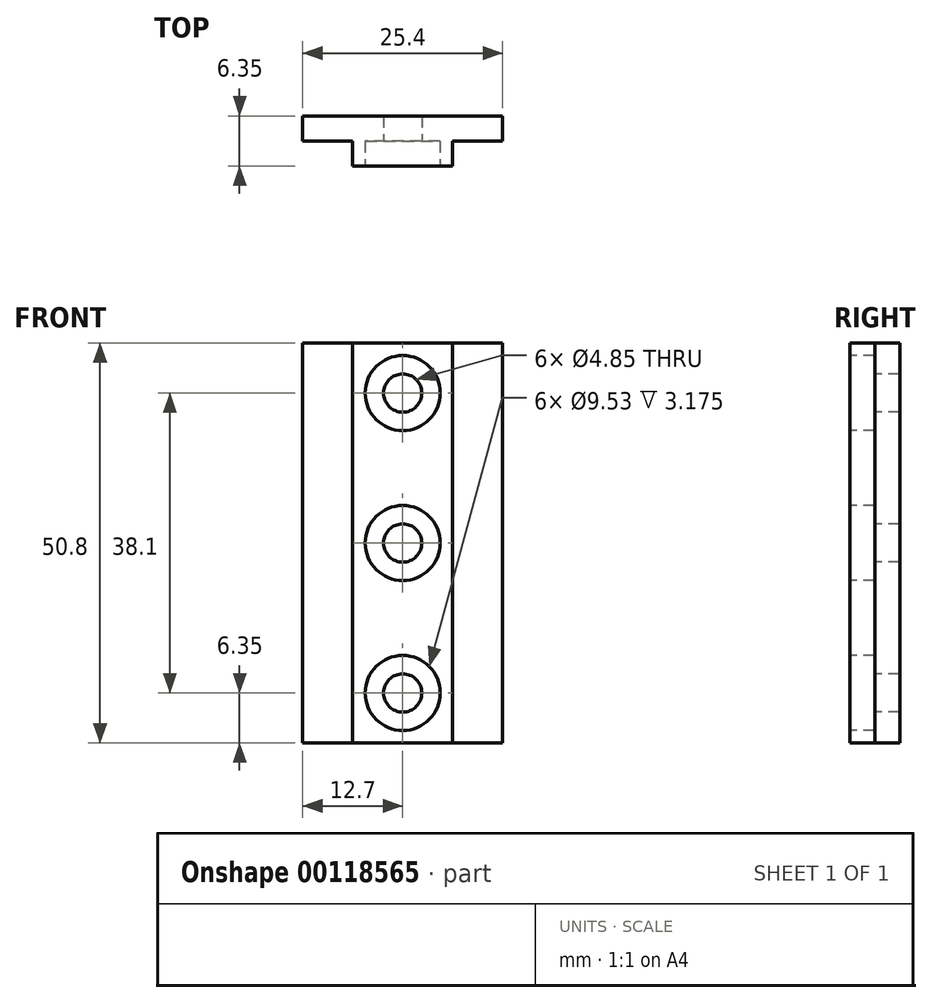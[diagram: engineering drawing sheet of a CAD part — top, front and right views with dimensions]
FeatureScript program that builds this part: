
annotation { "Feature Type Name" : "Feature", "Feature Type Description" : "" }
export const myFeature = defineFeature(function(context is Context, id is Id, definition is map)
    precondition{}
    {
        {
            var Q0;
            Q0=qCreatedBy(makeId("Front.planeOp"),FACE);
            var sketch = newSketch(context, id + "F0", { "sketchPlane" : qUnion([Q0])});
            skLineSegment(sketch, "E0.bottom", {"start": v(12.7, 25.4) * mm, "end": v(-12.7, 25.4) * mm});
            skLineSegment(sketch, "E0.top", {"start": v(12.7, -25.4) * mm, "end": v(-12.7, -25.4) * mm});
            skLineSegment(sketch, "E0.left", {"start": v(12.7, 25.4) * mm, "end": v(12.7, -25.4) * mm});
            skLineSegment(sketch, "E0.right", {"start": v(-12.7, 25.4) * mm, "end": v(-12.7, -25.4) * mm});
            skPoint(sketch, "E0.middle", {"position": v(0, 0) * mm});
            skSolve(sketch);
        }
        {
            var Q0;
            Q0 = qSketchRegion(id + "F0", true);
            extrude(context, id + "F1", {"entities" : qUnion([Q0]), "depth" : 6.35 * mm});
        }
        {
            var Q0;
            Q0=makeQuery(id+"F1.opExtrude","CAP_FACE",FACE,{"disambiguationData":[OSD([sQuery(id+"F0.wireOp",EDGE,"E0.bottom"),sQuery(id+"F0.wireOp",EDGE,"E0.top"),sQuery(id+"F0.wireOp",EDGE,"E0.left"),sQuery(id+"F0.wireOp",EDGE,"E0.right")])],"isStart":false});
            var sketch = newSketch(context, id + "F2", { "sketchPlane" : qUnion([Q0])});
            skLineSegment(sketch, "E1.bottom", {"start": v(6.35, 25.4) * mm, "end": v(-6.35, 25.4) * mm});
            skLineSegment(sketch, "E1.top", {"start": v(6.35, -25.4) * mm, "end": v(-6.35, -25.4) * mm});
            skLineSegment(sketch, "E1.left", {"start": v(6.35, 25.4) * mm, "end": v(6.35, -25.4) * mm});
            skLineSegment(sketch, "E1.right", {"start": v(-6.35, 25.4) * mm, "end": v(-6.35, -25.4) * mm});
            skPoint(sketch, "E1.middle", {"position": v(0, 0) * mm});
            skSolve(sketch);
        }
        {
            var Q0;
            {var subQ0=sQuery(id+"F2.wireOp",EDGE,"E1.right");Q0=makeQuery(id+"F2.imprint","IMPRINT",FACE,{"disambiguationData":[TD([[makeQuery(id+"F2.imprint","IMPRINT",EDGE,{"derivedFrom":subQ0}),-1.0]])]});}
            var Q1;
            {var subQ0=sQuery(id+"F2.wireOp",EDGE,"E1.left");Q1=makeQuery(id+"F2.imprint","IMPRINT",FACE,{"disambiguationData":[TD([[makeQuery(id+"F2.imprint","IMPRINT",EDGE,{"derivedFrom":subQ0}),1.0]])]});}
            extrude(context, id + "F3", {"entities" : qUnion([Q0, Q1]), "operationType" : NewBodyOperationType.REMOVE, "oppositeDirection" : true, "depth" : 3.17 * mm});
        }
        {
            var Q0;
            Q0=makeQuery(id+"F1.opExtrude","CAP_FACE",FACE,{"disambiguationData":[OSD([sQuery(id+"F0.wireOp",EDGE,"E0.bottom"),sQuery(id+"F0.wireOp",EDGE,"E0.top"),sQuery(id+"F0.wireOp",EDGE,"E0.left"),sQuery(id+"F0.wireOp",EDGE,"E0.right")])],"isStart":false});
            var sketch = newSketch(context, id + "F4", { "sketchPlane" : qUnion([Q0])});
            skCircle(sketch, "E2", {"center": v(0, 0) * mm, "radius": 2.43 * mm});
            skCircle(sketch, "E3", {"center": v(0, 19.05) * mm, "radius": 2.43 * mm});
            skCircle(sketch, "E4.MirrorC", {"center": v(0, -19.05) * mm, "radius": 2.43 * mm});
            skSolve(sketch);
        }
        {
            var Q0;
            Q0 = qSketchRegion(id + "F4", true);
            extrude(context, id + "F5", {"entities" : qUnion([Q0]), "operationType" : NewBodyOperationType.REMOVE, "endBound" : BoundingType.THROUGH_ALL, "oppositeDirection" : true, "depth" : 3.17 * mm});
        }
        {
            var Q0;
            Q0=makeQuery(id+"F1.opExtrude","CAP_FACE",FACE,{"disambiguationData":[OSD([sQuery(id+"F0.wireOp",EDGE,"E0.bottom"),sQuery(id+"F0.wireOp",EDGE,"E0.top"),sQuery(id+"F0.wireOp",EDGE,"E0.left"),sQuery(id+"F0.wireOp",EDGE,"E0.right")])],"isStart":false});
            var sketch = newSketch(context, id + "F6", { "sketchPlane" : qUnion([Q0])});
            skCircle(sketch, "E5", {"center": v(0, 19.05) * mm, "radius": 4.76 * mm});
            skCircle(sketch, "E6", {"center": v(0, 0) * mm, "radius": 4.76 * mm});
            skCircle(sketch, "E7", {"center": v(0, -19.05) * mm, "radius": 4.76 * mm});
            skSolve(sketch);
        }
        {
            var Q0;
            Q0 = qSketchRegion(id + "F6", true);
            extrude(context, id + "F7", {"entities" : qUnion([Q0]), "operationType" : NewBodyOperationType.REMOVE, "oppositeDirection" : true, "depth" : 3.17 * mm});
        }
        {
            var Q0;
            Q0=makeQuery(id+"F1.opExtrude","SWEPT_BODY",BODY,{"disambiguationData":[OSD([sQuery(id+"F0.wireOp",EDGE,"E0.bottom"),sQuery(id+"F0.wireOp",EDGE,"E0.top"),sQuery(id+"F0.wireOp",EDGE,"E0.left"),sQuery(id+"F0.wireOp",EDGE,"E0.right")])]});
            transform(context, id + "F8", {"entities" : qUnion([Q0]), "transformType" : TransformType.TRANSLATION_3D, "dx" : 0 * mm, "dy" : 0 * mm, "dz" : 0 * mm, "makeCopy" : true});
        }
    });
